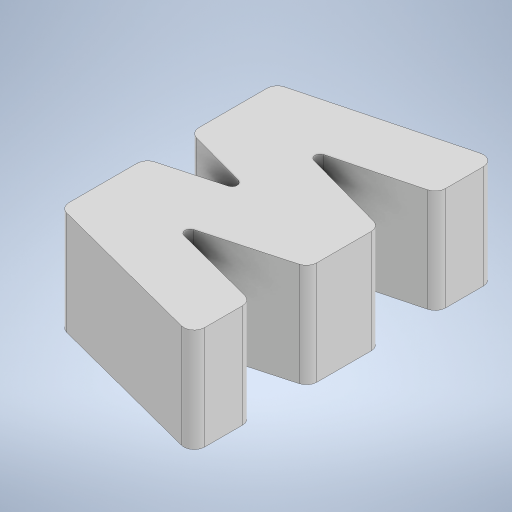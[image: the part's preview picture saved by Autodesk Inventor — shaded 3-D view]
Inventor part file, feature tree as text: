
AUTODESK INVENTOR PART (.ipt)
format: ipt  version: 2023 (Build 270158000, 158)  size: 370,176 bytes
history: native  units: mm
features: extrude x4, sketch x4, projected_geometry x3, other x2
ambient origin geometry x8: Origin, YZ Plane, XZ Plane, XY Plane, X Axis, Y Axis, Z Axis, Center Point
bodies: Body1 (feature_tree), Body2 (feature_tree)
feature tree (13):
  other  "contorno"
  extrude  "Extrusión1"  Depth=0.65mm
  extrude  "Extrusión2"  TaperAngle=30.0deg  [1 undecoded]
  extrude  "Extrusión3"  Depth=7.224mm
  extrude  "Extrusión4"  Depth=22.124mm
  sketch  "Boceto1"  dims[d8=13.0mm d9=0.0mm d17=0.65mm]
  sketch  "Boceto2"  dims[d41=1.3mm d42=30.0deg]
  projected_geometry  "Contorno proyectado1"
  other  "cavidad_cte"
  sketch  "Boceto3"  dims[d43=30.0deg d44=7.224mm]
  projected_geometry  "Contorno proyectado2"
  sketch  "Boceto4"  dims[d47=24.887mm d48=22.124mm d50=8.661mm d51=14.064mm d52=1.2mm d53=13.0mm d54=0.0mm d55=1.2mm d56=0.0mm d57=1.2mm d58=0.0mm]
  projected_geometry  "Contorno proyectado3"
note: 1 required parameter value undecoded (feature->parameter linkage not recoverable at this tier; creation-order binding heuristic only, values carry confidence <= 0.55)
